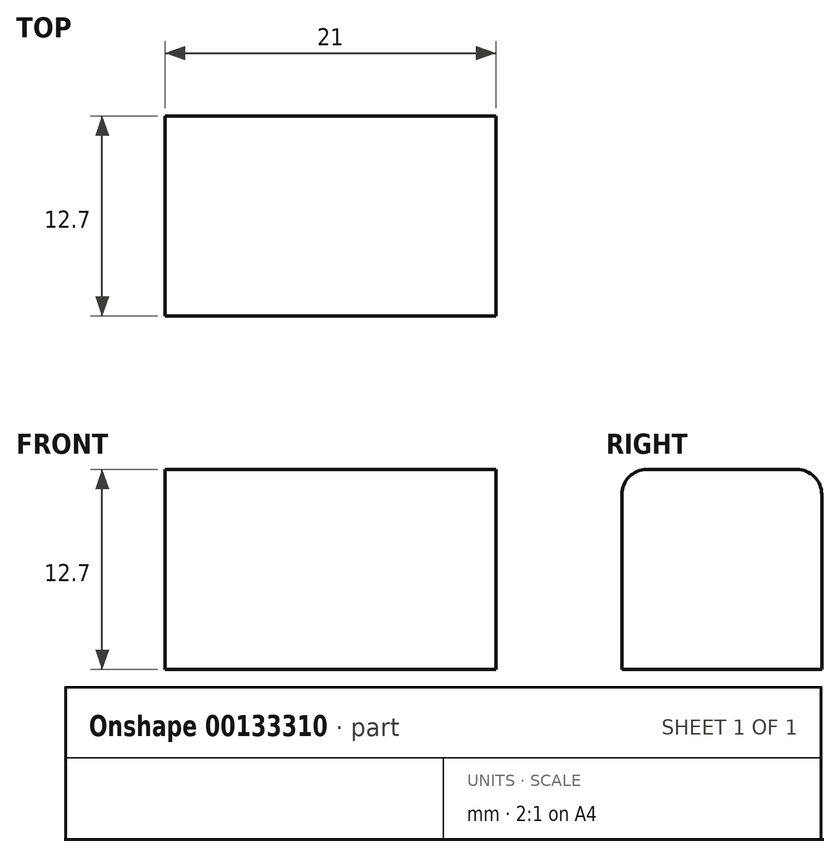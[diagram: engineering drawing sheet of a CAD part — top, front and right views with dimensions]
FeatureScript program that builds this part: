
annotation { "Feature Type Name" : "Feature", "Feature Type Description" : "" }
export const myFeature = defineFeature(function(context is Context, id is Id, definition is map)
    precondition{}
    {
        {
            assignVariable(context, id + "F0", {"name" : "W", "anyValue" : 24});
        }
        {
            var Q0;
            Q0=qCreatedBy(makeId("Right.planeOp"),FACE);
            var sketch = newSketch(context, id + "F1", { "sketchPlane" : qUnion([Q0])});
            skLineSegment(sketch, "E0.bottom", {"start": v(6.35, -6.35) * mm, "end": v(-6.35, -6.35) * mm});
            skLineSegment(sketch, "E0.top", {"start": v(4.76, 6.35) * mm, "end": v(-4.76, 6.35) * mm});
            skLineSegment(sketch, "E0.left", {"start": v(6.35, -6.35) * mm, "end": v(6.35, 4.76) * mm});
            skLineSegment(sketch, "E0.right", {"start": v(-6.35, -6.35) * mm, "end": v(-6.35, 4.76) * mm});
            skPoint(sketch, "E0.middle", {"position": v(0, 0) * mm});
            skPoint(sketch, "E1.visualSharp", {"position": v(-6.35, 6.35) * mm});
            skArc(sketch, "E1.filletArc", {"start": v(-4.76, 6.35) * mm, "mid": v(-5.89, 5.89) * mm, "end": v(-6.35, 4.76) * mm});
            skPoint(sketch, "E2.visualSharp", {"position": v(6.35, 6.35) * mm});
            skArc(sketch, "E2.filletArc", {"start": v(6.35, 4.76) * mm, "mid": v(5.89, 5.89) * mm, "end": v(4.76, 6.35) * mm});
            skSolve(sketch);
        }
        {
            var Q0;
            Q0=makeQuery(id+"F1.imprint","IMPRINT",FACE,{"disambiguationData":[TD([[makeQuery(id+"F1.imprint","IMPRINT",EDGE,{"derivedFrom":sQuery(id+"F1.wireOp",EDGE,"E0.bottom")}),-1.0]])]});
            extrude(context, id + "F2", {"entities" : qUnion([Q0]), "oppositeDirection" : true, "depth" : (getVariable(context, 'W') - 3) * mm});
        }
    });
